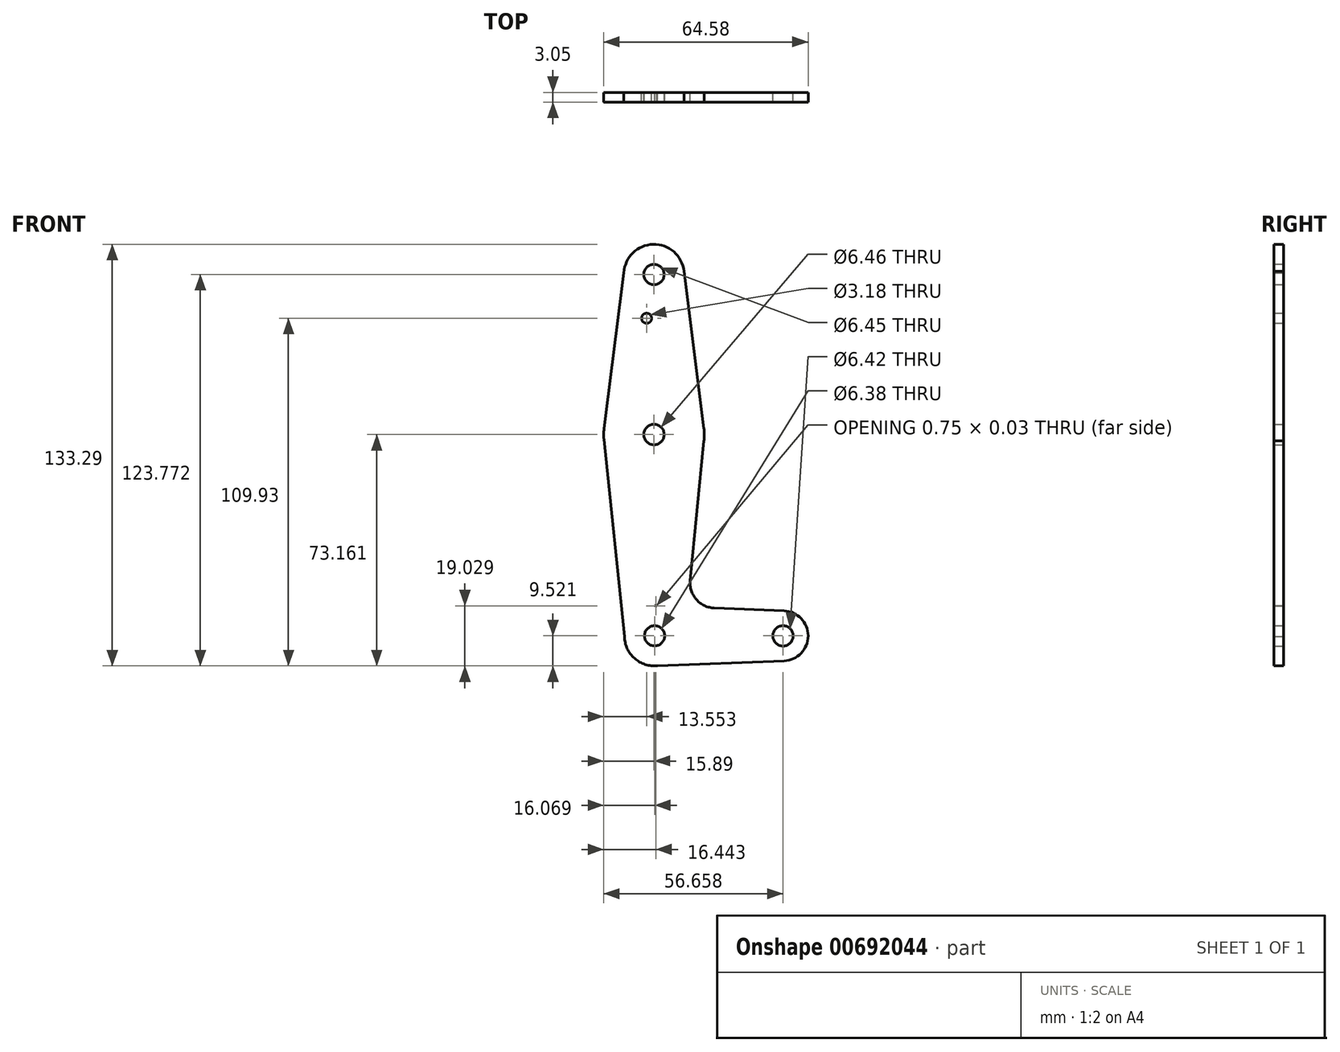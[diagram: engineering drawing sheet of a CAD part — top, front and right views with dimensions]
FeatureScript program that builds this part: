
annotation { "Feature Type Name" : "Feature", "Feature Type Description" : "" }
export const myFeature = defineFeature(function(context is Context, id is Id, definition is map)
    precondition{}
    {
        {
            var Q0;
            Q0=qCreatedBy(makeId("Front.planeOp"),FACE);
            var sketch = newSketch(context, id + "F0", { "sketchPlane" : qUnion([Q0])});
            skLineSegment(sketch, "E0", {"start": v(0, 0) * mm, "end": v(0, 3.36) * mm});
            skCircle(sketch, "E1", {"center": v(0, 114.42) * mm, "radius": 9.52 * mm});
            skArc(sketch, "E2", {"start": v(0.93, 9.66) * mm, "mid": v(0.46, 9.69) * mm, "end": v(0, 9.7) * mm});
            skLineSegment(sketch, "E3", {"start": v(0.18, 0.17) * mm, "end": v(40.77, 0.17) * mm});
            skCircle(sketch, "E4", {"center": v(40.77, 0.17) * mm, "radius": 7.92 * mm});
            skCircle(sketch, "E5", {"center": v(0, 63.81) * mm, "radius": 15.89 * mm});
            skLineSegment(sketch, "E6", {"start": v(-9.5, 114.96) * mm, "end": v(-15.76, 65.82) * mm});
            skLineSegment(sketch, "E7", {"start": v(9.47, 115.46) * mm, "end": v(15.76, 65.8) * mm});
            skLineSegment(sketch, "E8", {"start": v(15.76, 61.81) * mm, "end": v(11.45, 17.67) * mm});
            skLineSegment(sketch, "E9", {"start": v(-9.34, 0) * mm, "end": v(-15.8, 62.17) * mm});
            skLineSegment(sketch, "E10", {"start": v(0.18, 9.7) * mm, "end": v(0.93, 9.66) * mm});
            skLineSegment(sketch, "E11", {"start": v(0, -9.35) * mm, "end": v(41.08, -7.75) * mm});
            skCircle(sketch, "E12", {"center": v(0, 114.42) * mm, "radius": 3.23 * mm});
            skCircle(sketch, "E13", {"center": v(0, 63.81) * mm, "radius": 3.23 * mm});
            skCircle(sketch, "E14", {"center": v(40.77, 0.17) * mm, "radius": 3.2 * mm});
            skLineSegment(sketch, "E15", {"start": v(0, 63.81) * mm, "end": v(0, 100.4) * mm});
            skCircle(sketch, "E16", {"center": v(-2.34, 100.58) * mm, "radius": 1.59 * mm});
            skLineSegment(sketch, "E17.trimOffspring", {"start": v(19.06, 8.95) * mm, "end": v(41.08, 8.09) * mm});
            skLineSegment(sketch, "E18.trimOffspring", {"start": v(9.75, 0.17) * mm, "end": v(9.73, 0) * mm});
            skPoint(sketch, "E19.visualSharp", {"position": v(10.64, 9.28) * mm});
            skArc(sketch, "E19.filletArc", {"start": v(11.45, 17.67) * mm, "mid": v(13.38, 11.67) * mm, "end": v(19.06, 8.95) * mm});
            skCircle(sketch, "E20", {"center": v(0.18, 0.17) * mm, "radius": 3.2 * mm});
            skArc(sketch, "E21.trimOffspring", {"start": v(-9.34, 0) * mm, "mid": v(-6.16, -6.94) * mm, "end": v(1.1, -9.3) * mm});
            skLineSegment(sketch, "E22.trimOffspring", {"start": v(0, 9.7) * mm, "end": v(0, 114.42) * mm});
            skSolve(sketch);
        }
        {
            var Q0;
            Q0 = qSketchRegion(id + "F0", true);
            extrude(context, id + "F1", {"entities" : qUnion([Q0]), "depth" : 3.05 * mm, "offsetDistance" : 25.4 * mm});
        }
    });
